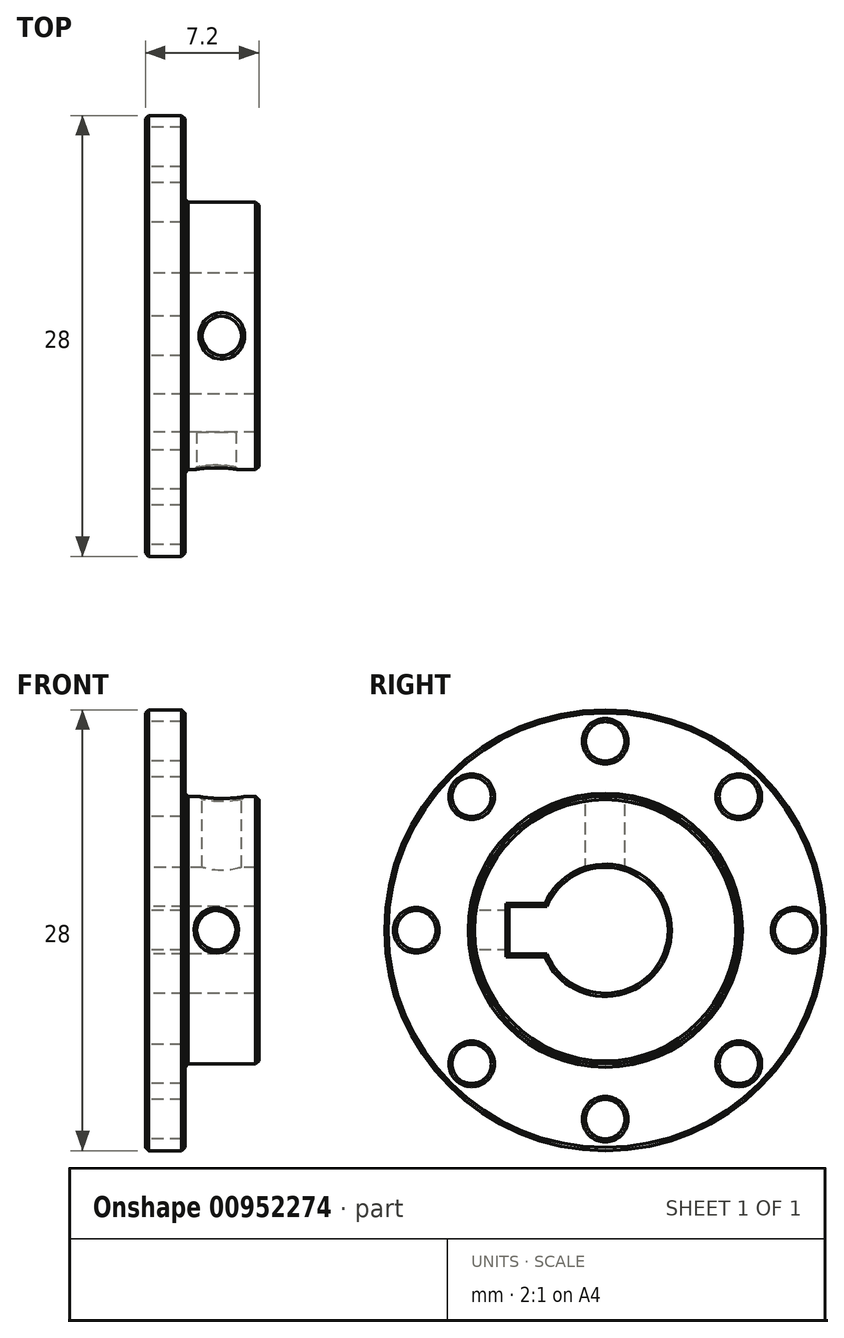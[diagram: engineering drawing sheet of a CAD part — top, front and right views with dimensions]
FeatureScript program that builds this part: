
annotation { "Feature Type Name" : "Feature", "Feature Type Description" : "" }
export const myFeature = defineFeature(function(context is Context, id is Id, definition is map)
    precondition{}
    {
        {
            var Q0;
            Q0=qCreatedBy(makeId("Top.planeOp"),FACE);
            cPlane(context, id + "F0", {"entities" : qUnion([Q0]), "cplaneType" : CPlaneType.OFFSET, "offset" : 0 * mm, "width" : 150 * mm, "height" : 150 * mm});
        }
        {
            var Q0;
            Q0=qCreatedBy(id+"F0.planeOp",FACE);
            var sketch = newSketch(context, id + "F1", { "sketchPlane" : qUnion([Q0])});
            skLineSegment(sketch, "E0", {"start": v(23.8, 8.5) * mm, "end": v(19.1, 8.5) * mm});
            skLineSegment(sketch, "E1", {"start": v(19.1, 8.5) * mm, "end": v(19.1, 14) * mm});
            skLineSegment(sketch, "E2", {"start": v(19.1, 14) * mm, "end": v(16.6, 14) * mm});
            skLineSegment(sketch, "E3", {"start": v(16.6, 14) * mm, "end": v(16.6, 5) * mm});
            skLineSegment(sketch, "E4", {"start": v(16.6, 4) * mm, "end": v(23.8, 4) * mm});
            skLineSegment(sketch, "E5", {"start": v(23.8, 4) * mm, "end": v(23.8, 8.5) * mm});
            skLineSegment(sketch, "E6", {"start": v(3.53, 0) * mm, "end": v(39.3, 0) * mm, "construction": true});
            skLineSegment(sketch, "E7", {"start": v(16.6, 5) * mm, "end": v(16.6, 4) * mm});
            skSolve(sketch);
        }
        {
            var Q0;
            Q0 = qSketchRegion(id + "F1", true);
            var Q1;
            Q1=sQuery(id+"F1.wireOp",EDGE,"E6");
            revolve(context, id + "F2", {"surfaceOperationType" : NewSurfaceOperationType.NEW, "entities" : qUnion([Q0]), "axis" : qUnion([Q1]), "revolveType" : RevolveType.FULL});
        }
        {
            var Q0;
            Q0=qCreatedBy(makeId("Right.planeOp"),FACE);
            cPlane(context, id + "F3", {"entities" : qUnion([Q0]), "cplaneType" : CPlaneType.OFFSET, "offset" : 16.6 * mm, "width" : 150 * mm, "height" : 150 * mm});
        }
        {
            var Q0;
            Q0=qCreatedBy(id+"F3.planeOp",FACE);
            var sketch = newSketch(context, id + "F4", { "sketchPlane" : qUnion([Q0])});
            skCircle(sketch, "E8", {"center": v(0, -12) * mm, "radius": 1.25 * mm});
            skCircle(sketch, "E9", {"center": v(0, 12) * mm, "radius": 1.25 * mm});
            skCircle(sketch, "E10", {"center": v(0, 0) * mm, "radius": 12 * mm, "construction": true});
            skCircle(sketch, "E11", {"center": v(12, 0) * mm, "radius": 1.25 * mm});
            skCircle(sketch, "E12", {"center": v(-12, 0) * mm, "radius": 1.25 * mm});
            skCircle(sketch, "E13.1.0", {"center": v(-8.49, 8.49) * mm, "radius": 1.25 * mm});
            skCircle(sketch, "E13.3.0", {"center": v(-8.49, -8.49) * mm, "radius": 1.25 * mm});
            skCircle(sketch, "E13.5.0", {"center": v(8.49, -8.49) * mm, "radius": 1.25 * mm});
            skCircle(sketch, "E13.7.0", {"center": v(8.49, 8.49) * mm, "radius": 1.25 * mm});
            skSolve(sketch);
        }
        {
            var Q0;
            Q0 = qSketchRegion(id + "F4", true);
            extrude(context, id + "F5", {"entities" : qUnion([Q0]), "operationType" : NewBodyOperationType.REMOVE, "depth" : 2.5 * mm, "offsetDistance" : 25 * mm});
        }
        {
            var Q0;
            Q0=qCreatedBy(makeId("Right.planeOp"),FACE);
            cPlane(context, id + "F6", {"entities" : qUnion([Q0]), "cplaneType" : CPlaneType.OFFSET, "offset" : 13 * mm, "width" : 150 * mm, "height" : 150 * mm});
        }
        {
            var Q0;
            Q0=qCreatedBy(id+"F6.planeOp",FACE);
            var sketch = newSketch(context, id + "F7", { "sketchPlane" : qUnion([Q0])});
            skLineSegment(sketch, "E14.bottom", {"start": v(-3, -1.5) * mm, "end": v(-6.1, -1.5) * mm});
            skLineSegment(sketch, "E14.top", {"start": v(-3, 1.5) * mm, "end": v(-6.1, 1.5) * mm});
            skLineSegment(sketch, "E14.left", {"start": v(-3, -1.5) * mm, "end": v(-3, 1.5) * mm});
            skLineSegment(sketch, "E14.right", {"start": v(-6.1, -1.5) * mm, "end": v(-6.1, 1.5) * mm});
            skLineSegment(sketch, "E15", {"start": v(-3, 0) * mm, "end": v(-7.05, 0) * mm, "construction": true});
            skPoint(sketch, "E15.endSnap0", {"position": v(-6, 0) * mm});
            skLineSegment(sketch, "E16", {"start": v(-4.55, -1.5) * mm, "end": v(-4.55, 3.33) * mm, "construction": true});
            skSolve(sketch);
        }
        {
            var Q0;
            Q0 = qSketchRegion(id + "F7", true);
            extrude(context, id + "F8", {"entities" : qUnion([Q0]), "operationType" : NewBodyOperationType.REMOVE, "endBound" : BoundingType.THROUGH_ALL, "depth" : 25 * mm, "offsetDistance" : 25 * mm});
        }
        {
            var Q0;
            Q0=qCreatedBy(makeId("Front.planeOp"),FACE);
            cPlane(context, id + "F9", {"entities" : qUnion([Q0]), "cplaneType" : CPlaneType.OFFSET, "offset" : 23 * mm, "width" : 150 * mm, "height" : 150 * mm});
        }
        {
            var Q0;
            Q0=qCreatedBy(id+"F9.planeOp",FACE);
            var sketch = newSketch(context, id + "F10", { "sketchPlane" : qUnion([Q0])});
            skCircle(sketch, "E17", {"center": v(21.1, 0) * mm, "radius": 1.25 * mm});
            skCircle(sketch, "E18", {"center": v(21.1, 0) * mm, "radius": 1.5 * mm, "construction": true});
            skSolve(sketch);
        }
        {
            var Q0;
            Q0 = qSketchRegion(id + "F10", true);
            extrude(context, id + "F11", {"entities" : qUnion([Q0]), "operationType" : NewBodyOperationType.REMOVE, "oppositeDirection" : true, "depth" : 17 * mm, "offsetDistance" : 25 * mm});
        }
        {
            var Q0;
            Q0=qCreatedBy(makeId("Top.planeOp"),FACE);
            cPlane(context, id + "F12", {"entities" : qUnion([Q0]), "cplaneType" : CPlaneType.OFFSET, "offset" : 13 * mm, "width" : 150 * mm, "height" : 150 * mm});
        }
        {
            var Q0;
            Q0=qCreatedBy(id+"F12.planeOp",FACE);
            var sketch = newSketch(context, id + "F13", { "sketchPlane" : qUnion([Q0])});
            skCircle(sketch, "E19", {"center": v(21.45, 0) * mm, "radius": 1.25 * mm});
            skSolve(sketch);
        }
        {
            var Q0;
            Q0 = qSketchRegion(id + "F13", true);
            extrude(context, id + "F14", {"entities" : qUnion([Q0]), "operationType" : NewBodyOperationType.REMOVE, "oppositeDirection" : true, "depth" : 13 * mm, "offsetDistance" : 25 * mm});
        }
        {
            var Q0;
            Q0=makeQuery(id+"F2.opRevolve","SWEPT_FACE",FACE,{"disambiguationData":[OSD([sQuery(id+"F1.wireOp",EDGE,"E3"),sQuery(id+"F1.wireOp",EDGE,"E7")])]});
            var Q1;
            Q1=makeQuery(id+"F2.opRevolve","SWEPT_FACE",FACE,{"disambiguationData":[OSD([sQuery(id+"F1.wireOp",EDGE,"E1")])]});
            var Q2;
            Q2=makeQuery(id+"F2.opRevolve","SWEPT_FACE",FACE,{"disambiguationData":[OSD([sQuery(id+"F1.wireOp",EDGE,"E5")])]});
            var Q3;
            Q3=makeQuery(id+"F2.opRevolve","SWEPT_FACE",FACE,{"disambiguationData":[OSD([sQuery(id+"F1.wireOp",EDGE,"E0")])]});
            var Q4;
            Q4=makeQuery(id+"F2.opRevolve","SWEPT_FACE",FACE,{"disambiguationData":[OSD([sQuery(id+"F1.wireOp",EDGE,"E2")])]});
            chamfer(context, id + "F15", {"entities" : qUnion([Q0, Q1, Q2, Q3, Q4]), "width" : 0.2 * mm, "tangentPropagation" : true});
        }
    });
